# Revit family: Gira_222500
name_source: partatom
category: Elektroinstallationen
revit_build: Autodesk Revit 2017 (Build: 20160225_1515(x64)
units: mm (PartAtom-declared; Revit-internal decimal feet)

## family parameters
Basisbauteil = Fläche
Beim Laden mit Abzugskörper schneiden = Nein
Bemaßung runder Anschluss = Durchmesser verwenden
Beschriftungsausrichtung beibehalten = Nein
Gemeinsam genutzt = Nein
Raumberechnungspunkt = Nein
Teiletyp = Normal

## types (1)
- Gira_222500
    BIM = https://media.stage.bim.site
    Beschreibung = Pres.det.Mini Kmf KNX,KNX presence detector - Mini Komfort,,,Presence detector for presence monitoring (operating mode: presence detector), for motion detection (operating mode: ceiling sentinel) or for monitoring with alarm telegrams (operating mode: alarm device) indoors or outdoors. With their subtle and flat design and flexible installation concept, presence detectors Mini are particularly suitable for properties with high architectural demands.,,Features:,- Extreme flat installation.,- Terminal mounting on suspended ceilings.,- Ceiling mounting on stable ceilings in device box in accordance with DIN 49073 using optional accessories.,- Surface mounted installation in surface-mounted box (optional accessories).,- Protection type IP44 allows installation outdoors and in humid rooms.,- The colour emphasis of the design rings enables their colours to be adapted to the wall or ceiling.,- When the design ring has been removed, all the operating elements (e.g. the programming button) of the device can be conveniently accessed from the front. Thus, removal is not necessary for subsequent adjustment or programming via the ETS.,- Ceiling-mounted device with integrated KNX bus coupler.,- PIR sensors: three sensors, integrated brightness sensor.,- Sensitivity of the motion detection can be set manually using an adjuster.,- Sensitivity can be configured by ETS.,- Sensitivity adjuster on the device can be deactivated using the software.,- Indication of motion detection (permanent or only during walking test).,- Separate evaluation in the long range of the three PIR sensors with 120 detection range each with overlapping.,- Manual actuation using IR remote control.,- A maximum of 5 + 2 function blocks are configurable.,- Functions that can be set for each function block 1 to 5: ceiling sentinel, presence detector, signal mode.,- Function block 6: presence detector with light control.,- Function block 7: brightness sensor with limit value monitoring.,- Function block changeover, e.g. for day night mode or weekday weekend operation.,- Function blocks 1 to 5: individual device, main unit, auxiliary unit can be set.,- Operating modes which can be set for individual device as a main unit: automatic, semi-automatic (manual ON   automatic OFF, or automatic ON   manual OFF).,- Two outputs per function block (1 to 5) for function ceiling sentinel, presence detector.,- Functions of ceiling sentinel, presence detector per output: switching, staircase function, switching with forced setting, dimming value transmitter, light scene auxiliary unit, temperature value transmitter, brightness value transmitter, temperature operating mode.,- Ceiling sentinel, presence detector: Twilight stage can be set via external communication object or per teach-in, additional transmission delay via external communication object, adaptive delay time (self-teaching additional transmission delay), short-term presence function, feedback of twilight stage, block function, manual operation using pushbutton sensor (separate communication object), switch-off brightness (for presence detectors) via teach-in, measurement of time period after last motion.,- Function of presence detector with light control: combination with function block of presence detector or individual device, setpoint value can be set, setpoint value specified via external communication object, setpoint offset via external communication object, teach-in function, feedback of the effective setpoint value.,- Function of brightness sensor with limit value monitoring: up to three limit values are configurable, functions of switching, dimming value transmitter, light scene auxiliary unit, configurable hysteresis, limit value via external communication object or teach-in, block function.,,Notes :,- The presence detector Mini is not suitable for alarm messages in VdS-compliant alarm systems.
    Bus system KNX = Ja
    Bus system KNX radio = Nein
    Bus system LON = Nein
    Bus system Powernet = Nein
    Bus system radio frequent = Nein
    Colour = White
    Data sheet = https://katalog.gira.de
    GTIN = 4010337014690
    HAN = 222500
    Hersteller = Gira
    Material = Other
    Material quality = Other
    Model = Presence detector
    Mounting method = Surface mounted (plaster)
    Other bus systems = None
    Productwebsite = http://katalog.gira.de
    Surface finishing = Not applicable
    Surface protection = Other
    Transparent = Nein
    Typname = Pres.detec.Mini Komfort KNX
    URL = https://www.gira.de
    Vorgabe-Ansicht = 1219 mm

## geometry (parser evidence)
native form markers: Sweep x1
no freeform markers — native parametric forms only
